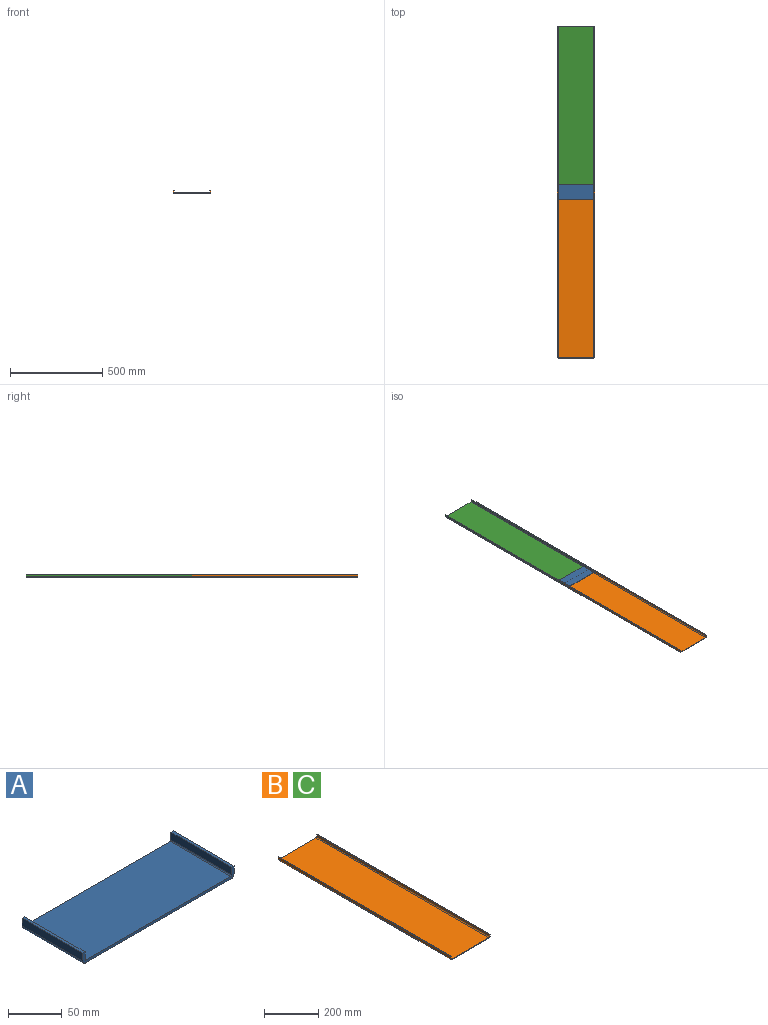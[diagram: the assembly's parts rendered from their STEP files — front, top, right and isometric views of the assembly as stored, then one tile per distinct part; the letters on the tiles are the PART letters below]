
ASSEMBLY  parts=3 mates=2
PART A: 14 faces, bbox 199x80x13 mm
  f0: plane 191x80mm, normal (0,0,1), area 15280mm2, adj f8,f9,f10,f11
  f1: plane 80x9mm, normal (1,0,0), area 720mm2, adj f2,f8,f9,f10
  f2: plane 80x3mm, normal (0,0,1), area 240mm2, adj f1,f3,f8,f9
  f3: plane 80x9mm, normal (-1,0,0), area 720mm2, adj f2,f8,f9,f12
  f4: plane 191x80mm, normal (0,0,-1), area 15280mm2, adj f8,f9,f12,f13
  f5: plane 80x9mm, normal (1,0,0), area 720mm2, adj f6,f8,f9,f13
  f6: plane 80x3mm, normal (0,0,1), area 240mm2, adj f5,f7,f8,f9
  f7: plane 80x9mm, normal (-1,0,0), area 720mm2, adj f6,f8,f9,f11
  f8: plane 199x13mm, normal (0,-1,0), area 650.6mm2, adj f0,f1,f2,f3,f4,f5,f6,f7
  f9: plane 199x13mm, normal (0,1,0), area 650.6mm2, adj f0,f1,f2,f3,f4,f5,f6,f7
  f10: cylinder r=1mm len=80mm, axis (0,-1,0), area 125.7mm2, adj f0,f1,f8,f9
  f11: cylinder r=1mm len=80mm, axis (0,1,0), area 125.7mm2, adj f0,f7,f8,f9
  f12: cylinder r=4mm len=80mm, axis (0,1,0), area 502.7mm2, adj f3,f4,f8,f9
  f13: cylinder r=4mm len=80mm, axis (0,-1,0), area 502.7mm2, adj f4,f5,f8,f9
PART B: 14 faces, bbox 205x900x16 mm
  f0: plane 900x9mm, normal (-1,0,0), area 8100mm2, adj f7,f8,f9,f10
  f1: plane 900x191mm, normal (0,0,1), area 171900mm2, adj f8,f9,f10,f11
  f2: plane 900x9mm, normal (1,0,0), area 8100mm2, adj f3,f8,f9,f11
  f3: plane 900x3mm, normal (0,0,1), area 2700mm2, adj f2,f4,f8,f9
  f4: plane 900x9mm, normal (-1,0,0), area 8100mm2, adj f3,f8,f9,f12
  f5: plane 900x191mm, normal (0,0,-1), area 171900mm2, adj f8,f9,f12,f13
  f6: plane 900x9mm, normal (1,0,0), area 8100mm2, adj f7,f8,f9,f13
  f7: plane 900x3mm, normal (0,0,1), area 2700mm2, adj f0,f6,f8,f9
  f8: plane 205x16mm, normal (0,-1,0), area 678.8mm2, adj f0,f1,f2,f3,f4,f5,f6,f7
  f9: plane 205x16mm, normal (0,1,0), area 678.8mm2, adj f0,f1,f2,f3,f4,f5,f6,f7
  f10: cylinder r=4mm len=900mm, axis (0,1,0), area 5654.9mm2, adj f0,f1,f8,f9
  f11: cylinder r=4mm len=900mm, axis (0,-1,0), area 5654.9mm2, adj f1,f2,f8,f9
  f12: cylinder r=7mm len=900mm, axis (0,1,0), area 9896mm2, adj f4,f5,f8,f9
  f13: cylinder r=7mm len=900mm, axis (0,-1,0), area 9896mm2, adj f5,f6,f8,f9
PART C: same geometry as B
PLACE A t=(164.29,484.76,-82.13)mm
PLACE B t=(164.29,34.76,-82.13)mm
PLACE C t=(164.29,934.76,-82.13)mm
MATE planar C.f8 <-> B.f9  axis (0,-1,0) through (164.29,484.76,-95.69)mm
MATE planar A.f4 <-> C.f1  axis (0,0,-1) through (164.29,484.76,-95.13)mm
